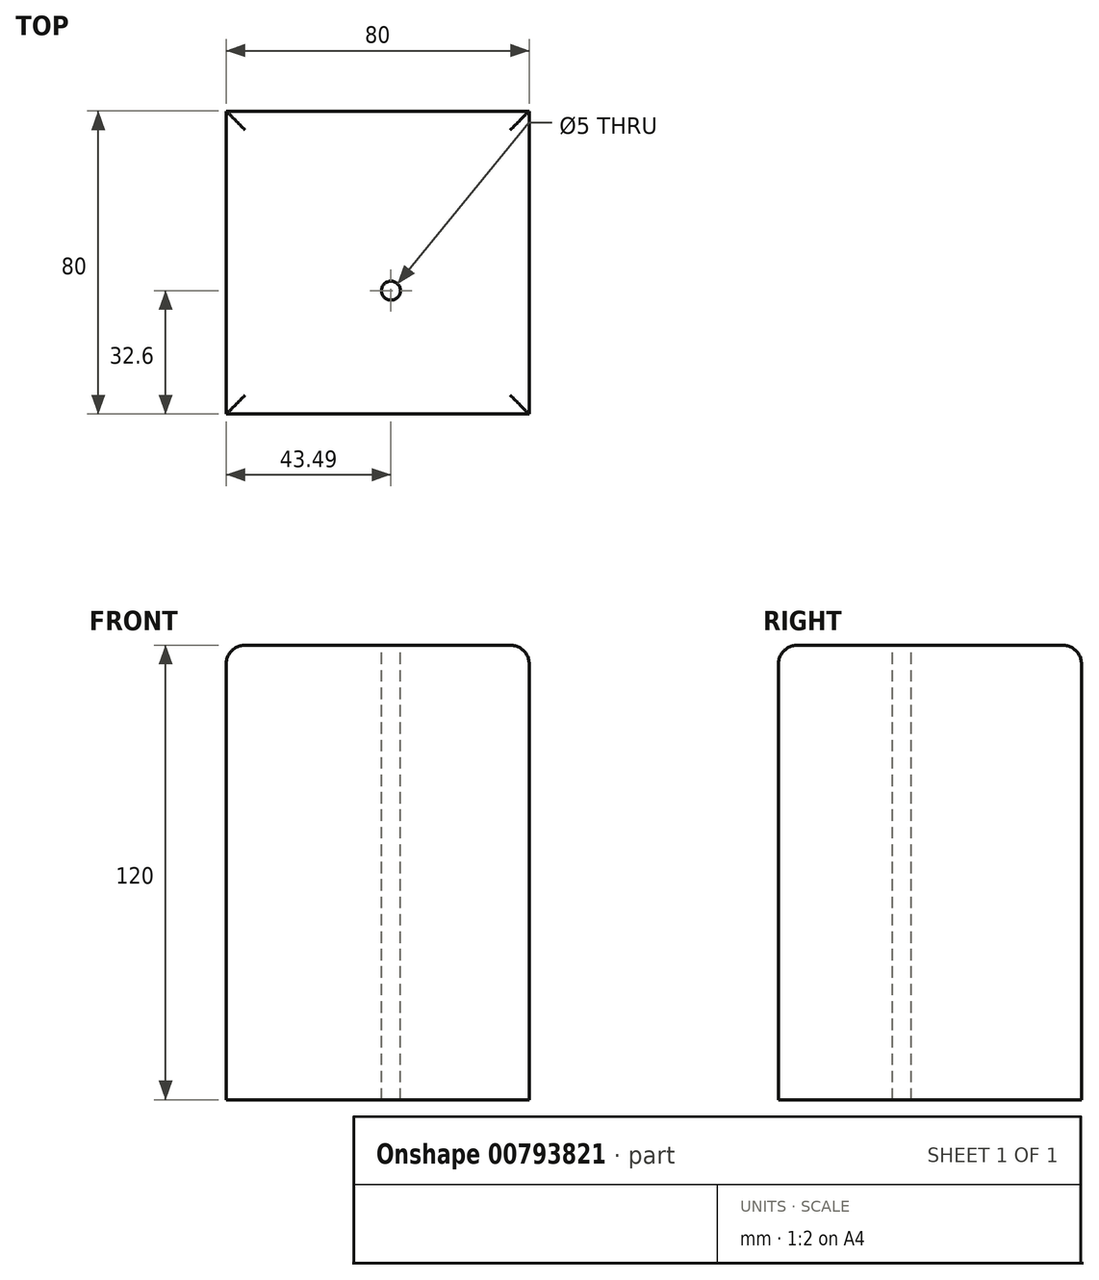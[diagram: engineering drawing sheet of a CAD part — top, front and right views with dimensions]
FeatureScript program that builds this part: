
annotation { "Feature Type Name" : "Feature", "Feature Type Description" : "" }
export const myFeature = defineFeature(function(context is Context, id is Id, definition is map)
    precondition{}
    {
        {
            var Q0;
            Q0=qCreatedBy(makeId("Top.planeOp"),FACE);
            var sketch = newSketch(context, id + "F0", { "sketchPlane" : qUnion([Q0])});
            skLineSegment(sketch, "E0.bottom", {"start": v(-43.5, 47.4) * mm, "end": v(36.5, 47.4) * mm});
            skLineSegment(sketch, "E0.top", {"start": v(-43.5, -32.6) * mm, "end": v(36.5, -32.6) * mm});
            skLineSegment(sketch, "E0.left", {"start": v(-43.5, 47.4) * mm, "end": v(-43.5, -32.6) * mm});
            skLineSegment(sketch, "E0.right", {"start": v(36.5, 47.4) * mm, "end": v(36.5, -32.6) * mm});
            skSolve(sketch);
        }
        {
            var Q0;
            Q0 = qSketchRegion(id + "F0", true);
            extrude(context, id + "F1", {"entities" : qUnion([Q0]), "depth" : 120 * mm, "offsetDistance" : 25 * mm});
        }
        {
            var Q0;
            Q0=makeQuery(id+"F1.opExtrude","CAP_EDGE",EDGE,{"disambiguationData":[OSD([sQuery(id+"F0.wireOp",EDGE,"E0.top")])],"isStart":false});
            var Q1;
            Q1=makeQuery(id+"F1.opExtrude","CAP_EDGE",EDGE,{"disambiguationData":[OSD([sQuery(id+"F0.wireOp",EDGE,"E0.right")])],"isStart":false});
            var Q2;
            Q2=makeQuery(id+"F1.opExtrude","CAP_EDGE",EDGE,{"disambiguationData":[OSD([sQuery(id+"F0.wireOp",EDGE,"E0.bottom")])],"isStart":false});
            var Q3;
            Q3=makeQuery(id+"F1.opExtrude","CAP_FACE",FACE,{"disambiguationData":[OSD([sQuery(id+"F0.wireOp",EDGE,"E0.bottom"),sQuery(id+"F0.wireOp",EDGE,"E0.top"),sQuery(id+"F0.wireOp",EDGE,"E0.left"),sQuery(id+"F0.wireOp",EDGE,"E0.right")])],"isStart":false});
            fillet(context, id + "F2", {"entities" : qUnion([Q0, Q1, Q2, Q3]), "radius" : 5 * mm, "tangentPropagation" : true, "allowEdgeOverflow" : false});
        }
        {
            var Q0;
            Q0=makeQuery(id+"F1.opExtrude","CAP_FACE",FACE,{"disambiguationData":[OSD([sQuery(id+"F0.wireOp",EDGE,"E0.bottom"),sQuery(id+"F0.wireOp",EDGE,"E0.top"),sQuery(id+"F0.wireOp",EDGE,"E0.left"),sQuery(id+"F0.wireOp",EDGE,"E0.right")])],"isStart":false});
            var sketch = newSketch(context, id + "F3", { "sketchPlane" : qUnion([Q0])});
            skCircle(sketch, "E1", {"center": v(0, 0) * mm, "radius": 15.23 * mm});
            skSolve(sketch);
        }
        {
            var Q0;
            Q0=sQuery(id+"F3.wireOp",VERTEX,"E1.center");
            var Q1;
            Q1=makeQuery(id+"F1.opExtrude","SWEPT_BODY",BODY,{"disambiguationData":[OSD([sQuery(id+"F0.wireOp",EDGE,"E0.bottom"),sQuery(id+"F0.wireOp",EDGE,"E0.top"),sQuery(id+"F0.wireOp",EDGE,"E0.left"),sQuery(id+"F0.wireOp",EDGE,"E0.right")])]});
            hole(context, id + "F4", {"style" : HoleStyle.SIMPLE, "endStyle" : HoleEndStyle.THROUGH, "holeDiameter" : 5 * mm, "majorDiameter" : 5 * mm, "isTappedThrough" : true, "tappedDepth" : 12 * mm, "tapClearance" : 3, "locations" : qUnion([Q0]), "scope" : qUnion([Q1])});
        }
    });
